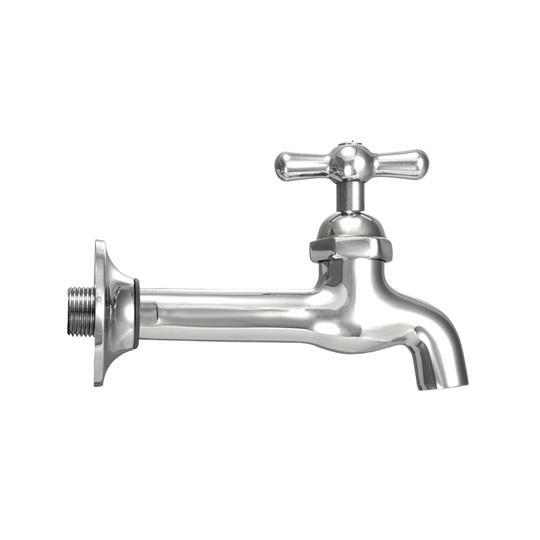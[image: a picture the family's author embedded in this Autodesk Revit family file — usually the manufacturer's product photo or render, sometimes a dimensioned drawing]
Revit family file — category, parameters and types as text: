
# Revit family: 01-9957-11 LLAVE EXTENSION TERMINAL METAL CROMO
name_source: partatom
category: Plumbing Fixtures
revit_build: Autodesk Revit 2018 (Build: 20170223_1515(x64)
units: mm (PartAtom-declared; Revit-internal decimal feet)

## family parameters
Cut with Voids When Loaded = No
Host = Face
OmniClass Number = 23.31.11.00
Part Type = Normal
Room Calculation Point = No
Round Connector Dimension = Use Diameter
Shared = No

## types (1)
- 01-9957-11
    Acometida = Dim 1/2" NPT
    Alto = 93 mm  [stored 0.305118 ft]
    Ancho = 163 mm
    Ancho manija llave = 60 mm  [stored 0.19685 ft]
    CW Connection = Yes
    Default Elevation = 0 mm  [stored 0 ft]
    Description = Llave jardin
    Dim Escudo = 60 mm  [stored 0.19685 ft]
    HW Connection = Yes
    Link Ficha Tecnica = http://infotecnica.gricol.com
    Manufacturer = Gricol
    Metal laton cromado = Metal Laton Cromado
    Model = 01-9957-11
    Product Name = LLAVE EXTENSION TERMINAL METAL CROMO
    Salida = Dim 3/4" NH
    Type Image = LLAVE EXTENSION TERMINAL METAL CROMO.jpg
    URL = https://www.gricol.com
    Vent Connection = No
    Waste Connection = No

note: [stored X ft] marks values corroborated as IEEE doubles in the binary element streams (Revit-internal decimal feet)

## geometry (parser evidence)
native form markers: Blend x2, Sweep x4
no freeform markers — native parametric forms only
